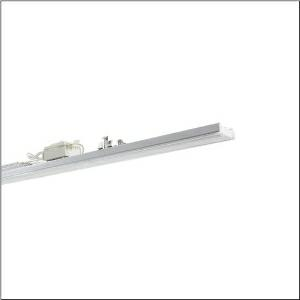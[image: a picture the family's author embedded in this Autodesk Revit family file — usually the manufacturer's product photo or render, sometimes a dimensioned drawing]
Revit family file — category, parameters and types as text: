
# Revit family: licross_11_recessed_ho_51tl12mv465m
name_source: partatom
category: Lighting Fixtures
units: mm (PartAtom-declared; Revit-internal decimal feet)

## family parameters
Cut with Voids When Loaded = No
Host = Face
Light Source = No
Part Type = Normal
Room Calculation Point = No
Round Connector Dimension = Use Diameter
Shared = No

## types (1)
- --- (1 x LED, 6990 lm, 34.4 W, 4000K)
    Apparent Load = 34 VA
    CIE Flux Codes = 66 91 98 100 100
    Color Rendering = 80
    Color Temperature = 4000K
    Default Elevation = 1800 mm
    Description = Licross 11 Recessed HO, luminaire insert, of sheet steel, coil coated, white, length: 2.250mm, width: 66mm, height: 67mm, LED rated luminous flux: 6.990lm, light colour: 840, SDCM (Standard Deviation of Colour Matching)MacAdam ≤ 2 SDCM (initial), control gear: ON/OFF Multilumen, with plug, 3-pole, with phase selection, mains connection: 220..240V, AC, 50/60Hz, rated input power: 34W, internal wiring halogen-free, primary optical cover: cover, of PMMA, light emission: direct distribution, primary light characteristic: symmetric, protection rating (complete): IP40, insulation class (complete): insulation class I (protective earthing), certification: CE, ENEC, VDE, UKCA, protection symbol: D if used in an environment without relevant dust loads with corresponding accessories, impact resistance: IK06, permissible ambient temperature for indoor applications: -35..+50°C, corresponds to IFS (International Featured Standards) requirements for safety and quality in the food industry, reducing of maximum allowable ambient temperature of 5°C with ceiling mounting, LABS conformity tested according to VDMA 24364:2018-05, The light source and the operating device comply with the requirements of the Ecodesign Regulation (EU) 2019/2020 and are replaceable in accordance with this regulation, packaging unit: 1 piece
    Height = 58 mm
    Lamp = 1 x LED
    Lamp Light Flux = 6990 lm
    Lamp Power = 34.4 W
    Lamp count = 1
    Length = 2250 mm
    Luminous efficacy = 203 lm/W
    Manufacturer = Siteco
    ModVariant = No
    Model = 51TL12MV465M
    Mounting Place = Ceiling
    Mounting Type = Pendant
    Number of Poles = 1
    OnlyDefault = Yes
    Power Factor = 1
    Product Name = Licross 11 Recessed HO
    Product group = luminaire insert | ceiling pendant
    ProductGroupID = 901
    Protection Class = Protection class I
    Protection Degree = IP 40
    RLX_Detail_Level = 1
    RLX_Emergency_Light_Flux = 0 lm
    RLX_Emergency_Type = 0
    RLX_Emergency_Type_DB = No
    RlxData = <blob elided: 27061 chars, md5=2b0cb7ef>
    Socket = socket
    Standby Power = 0 W
    System Light Flux = 6990 lm
    System Power = 34 W
    Type Comments = factory setting: luminous flux: 100 % | (A | C | E) | 82 mA
    Type Image = l_1296930.jpg
    URL = http://relux.com
    VarID = @adj_089879
    Voltage = 0 V
    Weight = 0.00 kg
    Width = 66 mm

## geometry (parser evidence)
native form markers: Blend x4, Sweep x10
no freeform markers — native parametric forms only
